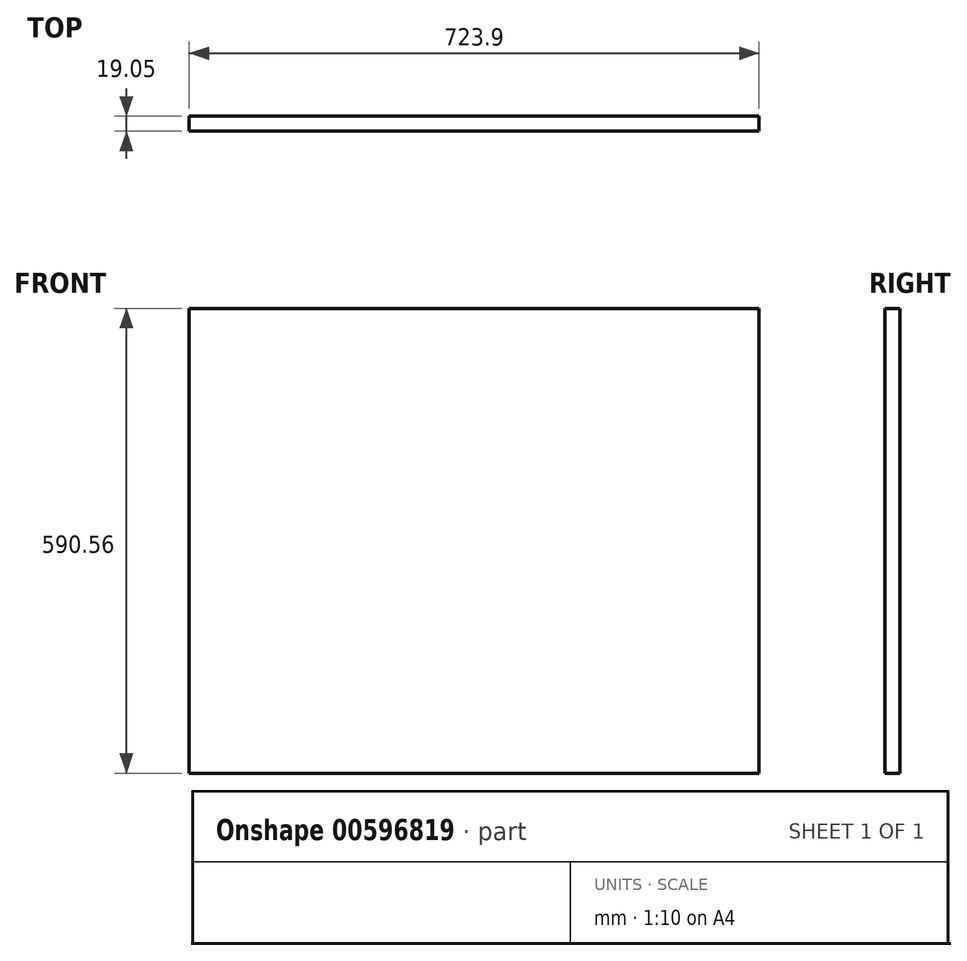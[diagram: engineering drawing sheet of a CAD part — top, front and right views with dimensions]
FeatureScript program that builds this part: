
annotation { "Feature Type Name" : "Feature", "Feature Type Description" : "" }
export const myFeature = defineFeature(function(context is Context, id is Id, definition is map)
    precondition{}
    {
        {
            var Q0;
            Q0=qCreatedBy(makeId("Front.planeOp"),FACE);
            var sketch = newSketch(context, id + "F0", { "sketchPlane" : qUnion([Q0])});
            skLineSegment(sketch, "E0.bottom", {"start": v(361.95, 295.28) * mm, "end": v(-361.95, 295.28) * mm});
            skLineSegment(sketch, "E0.top", {"start": v(361.95, -295.28) * mm, "end": v(-361.95, -295.28) * mm});
            skLineSegment(sketch, "E0.left", {"start": v(361.95, 295.28) * mm, "end": v(361.95, -295.28) * mm});
            skLineSegment(sketch, "E0.right", {"start": v(-361.95, 295.28) * mm, "end": v(-361.95, -295.28) * mm});
            skPoint(sketch, "E0.middle", {"position": v(0, 0) * mm});
            skSolve(sketch);
        }
        {
            var Q0;
            Q0=makeQuery(id+"F0.imprint","IMPRINT",FACE,{"disambiguationData":[TD([[makeQuery(id+"F0.imprint","IMPRINT",EDGE,{"derivedFrom":sQuery(id+"F0.wireOp",EDGE,"E0.bottom")}),1.0]])]});
            extrude(context, id + "F1", {"entities" : qUnion([Q0]), "depth" : 19.05 * mm, "offsetDistance" : 25.4 * mm});
        }
    });
